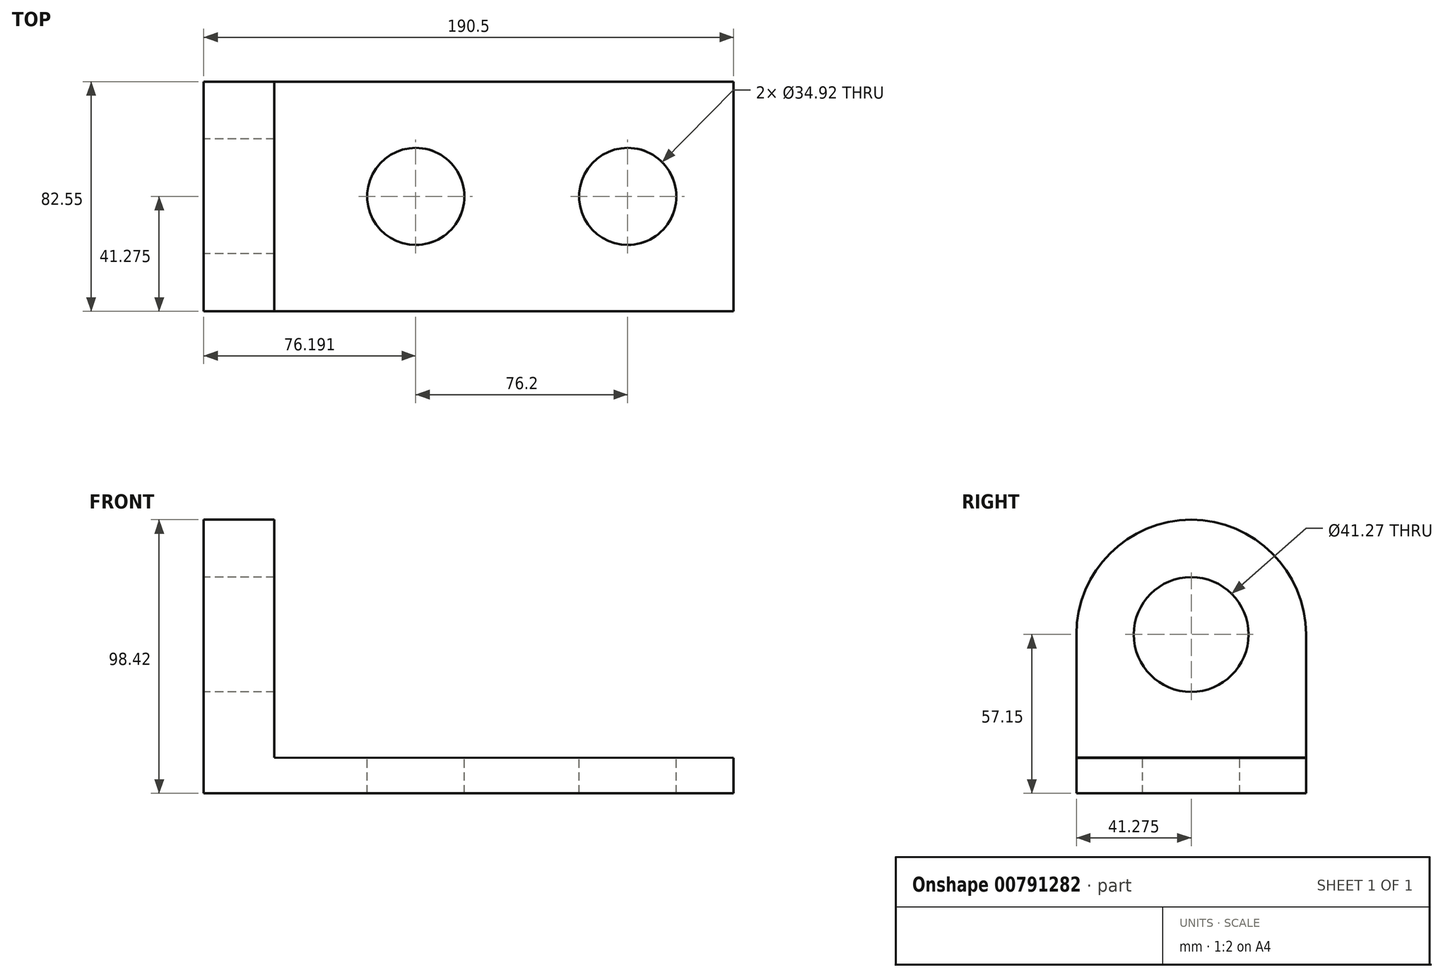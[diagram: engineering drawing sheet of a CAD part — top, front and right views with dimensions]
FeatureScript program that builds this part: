
annotation { "Feature Type Name" : "Feature", "Feature Type Description" : "" }
export const myFeature = defineFeature(function(context is Context, id is Id, definition is map)
    precondition{}
    {
        {
            var Q0;
            Q0=qCreatedBy(makeId("Front.planeOp"),FACE);
            var sketch = newSketch(context, id + "F0", { "sketchPlane" : qUnion([Q0])});
            skLineSegment(sketch, "E0", {"start": v(0, 0) * mm, "end": v(190.5, 0) * mm});
            skLineSegment(sketch, "E1", {"start": v(190.5, 0) * mm, "end": v(190.5, 12.7) * mm});
            skLineSegment(sketch, "E2", {"start": v(0, 0) * mm, "end": v(0, 114.3) * mm});
            skLineSegment(sketch, "E3", {"start": v(0, 114.3) * mm, "end": v(25.4, 114.3) * mm});
            skLineSegment(sketch, "E4", {"start": v(25.4, 114.3) * mm, "end": v(25.4, 12.92) * mm});
            skLineSegment(sketch, "E5", {"start": v(25.4, 12.92) * mm, "end": v(190.5, 12.7) * mm});
            skSolve(sketch);
        }
        {
            var Q0;
            Q0=makeQuery(id+"F0.imprint","IMPRINT",FACE,{"disambiguationData":[TD([[makeQuery(id+"F0.imprint","IMPRINT",EDGE,{"derivedFrom":sQuery(id+"F0.wireOp",EDGE,"E0")}),1.0]])]});
            extrude(context, id + "F1", {"entities" : qUnion([Q0]), "depth" : 82.55 * mm, "offsetDistance" : 25.4 * mm});
        }
        {
            var Q0;
            Q0=makeQuery(id+"F1.opExtrude","SWEPT_FACE",FACE,{"disambiguationData":[OSD([sQuery(id+"F0.wireOp",EDGE,"E2")])]});
            var sketch = newSketch(context, id + "F2", { "sketchPlane" : qUnion([Q0])});
            skLineSegment(sketch, "E6", {"start": v(0, 0) * mm, "end": v(0, 57.15) * mm});
            skLineSegment(sketch, "E7", {"start": v(82.55, 0) * mm, "end": v(82.55, 57.15) * mm});
            skArc(sketch, "E8", {"start": v(82.55, 57.15) * mm, "mid": v(41.27, 98.43) * mm, "end": v(0, 57.15) * mm});
            skCircle(sketch, "E9", {"center": v(41.27, 57.15) * mm, "radius": 20.64 * mm});
            skSolve(sketch);
        }
        {
            var Q0;
            Q0=makeQuery(id+"F2.imprint","IMPRINT",FACE,{"disambiguationData":[TD([[makeQuery(id+"F2.imprint","IMPRINT",EDGE,{"derivedFrom":sQuery(id+"F2.wireOp",EDGE,"E9")}),1.0]])]});
            var Q1;
            {var subQ0=sQuery(id+"F2.wireOp",EDGE,"E8");Q1=makeQuery(id+"F2.imprint","IMPRINT",FACE,{"disambiguationData":[TD([[makeQuery(id+"F2.imprint","IMPRINT",EDGE,{"derivedFrom":subQ0}),-1.0]])]});}
            extrude(context, id + "F3", {"entities" : qUnion([Q0, Q1]), "operationType" : NewBodyOperationType.REMOVE, "oppositeDirection" : true, "depth" : 152.4 * mm, "offsetDistance" : 25.4 * mm});
        }
        {
            var Q0;
            Q0=makeQuery(id+"F1.opExtrude","SWEPT_FACE",FACE,{"disambiguationData":[OSD([sQuery(id+"F0.wireOp",EDGE,"E5")])]});
            var sketch = newSketch(context, id + "F4", { "sketchPlane" : qUnion([Q0])});
            skLineSegment(sketch, "E10", {"start": v(190.48, -41.28) * mm, "end": v(152.38, -41.28) * mm, "construction": true});
            skLineSegment(sketch, "E11", {"start": v(152.38, -41.28) * mm, "end": v(76.18, -41.28) * mm, "construction": true});
            skCircle(sketch, "E12", {"center": v(76.18, -41.28) * mm, "radius": 17.46 * mm});
            skCircle(sketch, "E13", {"center": v(152.38, -41.28) * mm, "radius": 17.46 * mm});
            skSolve(sketch);
        }
        {
            var Q0;
            Q0 = qSketchRegion(id + "F4", true);
            extrude(context, id + "F5", {"entities" : qUnion([Q0]), "operationType" : NewBodyOperationType.REMOVE, "oppositeDirection" : true, "depth" : 25.4 * mm, "offsetDistance" : 25.4 * mm});
        }
    });
